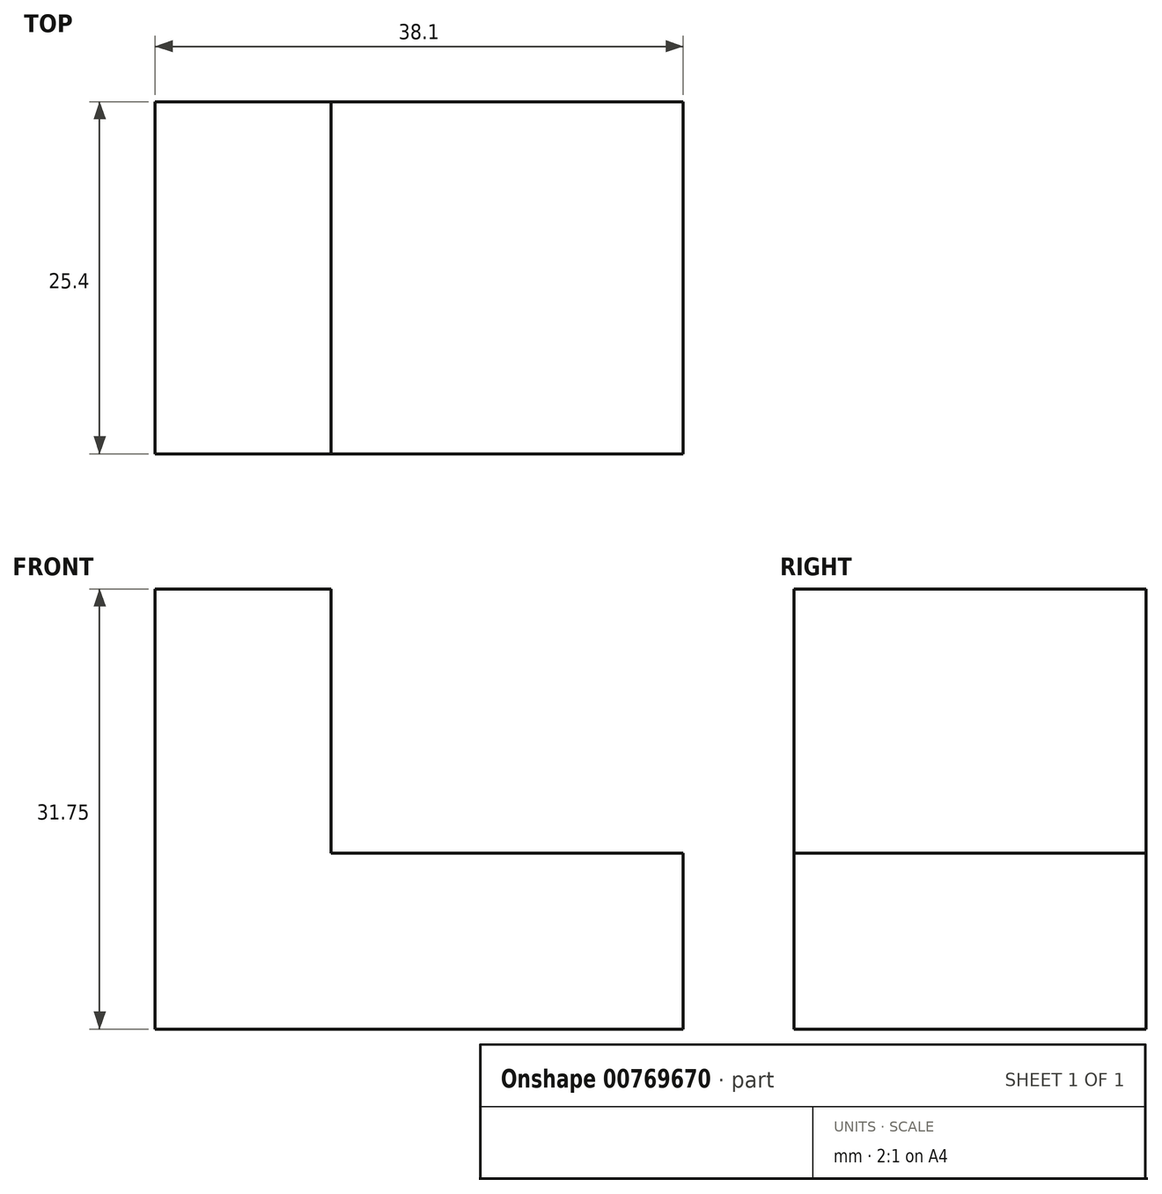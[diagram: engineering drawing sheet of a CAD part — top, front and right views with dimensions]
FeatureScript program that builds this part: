
annotation { "Feature Type Name" : "Feature", "Feature Type Description" : "" }
export const myFeature = defineFeature(function(context is Context, id is Id, definition is map)
    precondition{}
    {
        {
            var Q0;
            Q0=qCreatedBy(makeId("Front.planeOp"),FACE);
            var sketch = newSketch(context, id + "F0", { "sketchPlane" : qUnion([Q0])});
            skLineSegment(sketch, "E0", {"start": v(38.1, 0) * mm, "end": v(0, 0) * mm});
            skLineSegment(sketch, "E1", {"start": v(0, 0) * mm, "end": v(0, 31.75) * mm});
            skLineSegment(sketch, "E2", {"start": v(0, 31.75) * mm, "end": v(12.7, 31.75) * mm});
            skLineSegment(sketch, "E3", {"start": v(12.7, 31.75) * mm, "end": v(12.7, 12.7) * mm});
            skLineSegment(sketch, "E4", {"start": v(12.7, 12.7) * mm, "end": v(38.1, 12.7) * mm});
            skLineSegment(sketch, "E5", {"start": v(38.1, 0) * mm, "end": v(38.1, 12.7) * mm});
            skSolve(sketch);
        }
        {
            var Q0;
            Q0 = qSketchRegion(id + "F0", true);
            extrude(context, id + "F1", {"entities" : qUnion([Q0]), "depth" : 25.4 * mm, "offsetDistance" : 25.4 * mm});
        }
    });
